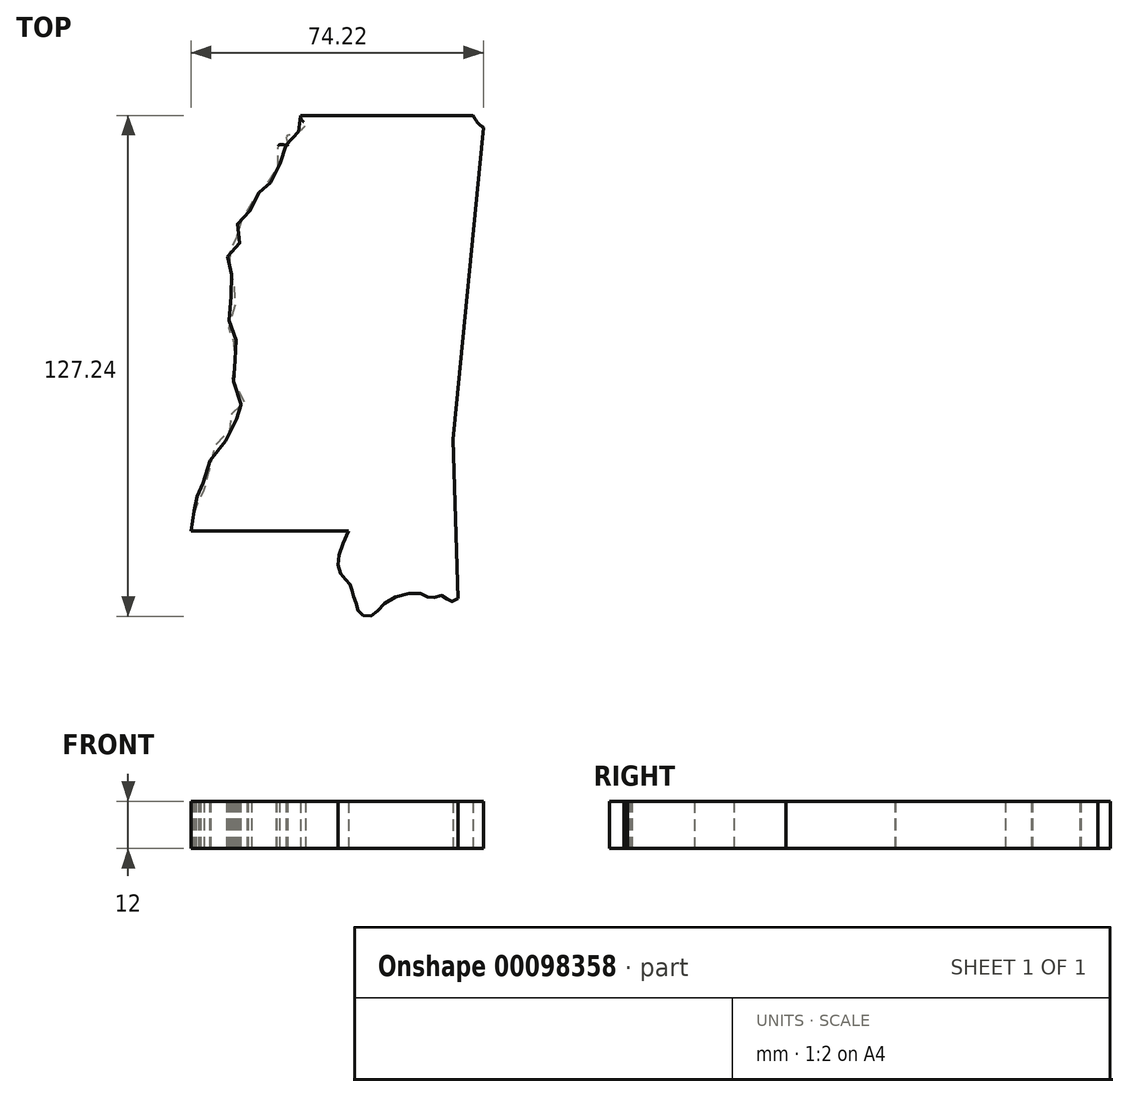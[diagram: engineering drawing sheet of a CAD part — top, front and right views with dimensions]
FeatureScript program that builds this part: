
annotation { "Feature Type Name" : "Feature", "Feature Type Description" : "" }
export const myFeature = defineFeature(function(context is Context, id is Id, definition is map)
    precondition{}
    {
        {
            var Q0;
            Q0=qCreatedBy(makeId("Top.planeOp"),FACE);
            var sketch = newSketch(context, id + "F0", { "sketchPlane" : qUnion([Q0])});
            skLineSegment(sketch, "E0", {"start": v(-12.7, 63.77) * mm, "end": v(31.18, 63.77) * mm});
            skFitSpline(sketch, "E1", {"points": [v(31.18, 63.77) * mm, v(32.21, 62.04) * mm, v(33.76, 60.7) * mm], "startDerivative": vector(1.8, -3.72) * mm, "endDerivative": vector(3.34, -2.47) * mm});
            skLineSegment(sketch, "E2", {"start": v(33.76, 60.7) * mm, "end": v(26.03, -18.61) * mm});
            skLineSegment(sketch, "E3", {"start": v(26.03, -18.61) * mm, "end": v(27.37, -58.89) * mm});
            skFitSpline(sketch, "E4", {"points": [v(27.37, -58.89) * mm, v(25.31, -59.72) * mm, v(23.35, -58.18) * mm, v(20.47, -58.89) * mm, v(17.78, -57.7) * mm, v(9.08, -59.84) * mm, v(5.6, -63.23) * mm, v(2.34, -62.72) * mm, v(1.36, -59.9) * mm, v(0.5, -57.7) * mm, v(0, -55.49) * mm, v(-2, -53.47) * mm, v(-3.17, -49.61) * mm, v(-0.53, -41.87) * mm], "startDerivative": vector(-36.12, -26.53) * mm, "endDerivative": vector(32.5, 71.75) * mm});
            skLineSegment(sketch, "E5", {"start": v(-0.53, -41.87) * mm, "end": v(-40.44, -41.87) * mm});
            skFitSpline(sketch, "E6", {"points": [v(-40.44, -41.87) * mm, v(-39.67, -39.77) * mm, v(-40.44, -38.7) * mm, v(-39.72, -37.05) * mm, v(-40.44, -35.23) * mm, v(-38.85, -34.85) * mm, v(-38.5, -34.05) * mm, v(-39.15, -32.33) * mm, v(-38.56, -31.67) * mm, v(-37.43, -31.59) * mm, v(-37.05, -30.55) * mm, v(-37.96, -28.15) * mm, v(-35.72, -26.44) * mm, v(-35.7, -23.45) * mm, v(-34.25, -20) * mm, v(-32.37, -19.7) * mm, v(-31.16, -17.3) * mm, v(-29.66, -15.02) * mm, v(-28.85, -13.64) * mm, v(-29.89, -12.26) * mm, v(-30.28, -10.96) * mm, v(-28.67, -9.86) * mm, v(-27.02, -9.23) * mm, v(-26.3, -7.13) * mm, v(-29.83, -3.53) * mm, v(-28.89, -0.89) * mm, v(-28.47, 0.56) * mm, v(-29.33, 1.72) * mm, v(-28.65, 2.87) * mm, v(-30.22, 4.64) * mm, v(-28.72, 7.26) * mm, v(-29.38, 9.32) * mm, v(-30.64, 9.26) * mm, v(-30.26, 13.36) * mm, v(-28.94, 14.62) * mm, v(-30.1, 17.48) * mm, v(-30.69, 18.55) * mm, v(-29.71, 20.5) * mm, v(-29.76, 22.92) * mm, v(-31.3, 24.16) * mm, v(-30.59, 25.58) * mm, v(-30.63, 27.17) * mm, v(-31.39, 28.43) * mm, v(-30.38, 29.35) * mm, v(-29.75, 30.33) * mm, v(-28.17, 31.25) * mm, v(-28.83, 33.24) * mm, v(-27.87, 34.55) * mm, v(-28.79, 35.9) * mm, v(-26.78, 37.23) * mm, v(-25.14, 37.45) * mm, v(-25.35, 38.95) * mm, v(-25.9, 40.42) * mm, v(-24.3, 42) * mm, v(-23.54, 44.18) * mm, v(-22.36, 43.96) * mm, v(-22.1, 45.63) * mm, v(-21.62, 46.62) * mm, v(-20.25, 46.74) * mm, v(-18.65, 47.92) * mm, v(-18.74, 49.65) * mm, v(-17.9, 51.6) * mm, v(-18.66, 53.8) * mm, v(-17.96, 56.35) * mm, v(-15.95, 56.25) * mm, v(-16.18, 58.35) * mm, v(-14.42, 59.18) * mm, v(-12.65, 60.1) * mm, v(-11.33, 61.65) * mm, v(-12.29, 62.48) * mm, v(-12.7, 63.77) * mm], "startDerivative": vector(163.3, 88.27) * mm, "endDerivative": vector(-8.55, 126.33) * mm});
            skLineSegment(sketch, "E7", {"start": v(17.74, 63.77) * mm, "end": v(17.04, -63.23) * mm, "construction": true});
            skSolve(sketch);
        }
        {
            var Q0;
            Q0 = qSketchRegion(id + "F0", true);
            extrude(context, id + "F1", {"entities" : qUnion([Q0]), "depth" : 2 * mm, "offsetDistance" : 25 * mm});
        }
        {
            var Q0;
            Q0=makeQuery(id+"F1.opExtrude","SWEPT_BODY",BODY,{"disambiguationData":[OSD([sQuery(id+"F0.wireOp",EDGE,"E0"),sQuery(id+"F0.wireOp",EDGE,"E1"),sQuery(id+"F0.wireOp",EDGE,"E2"),sQuery(id+"F0.wireOp",EDGE,"E3"),sQuery(id+"F0.wireOp",EDGE,"E4"),sQuery(id+"F0.wireOp",EDGE,"E5"),sQuery(id+"F0.wireOp",EDGE,"E6")])]});
            transform(context, id + "F2", {"entities" : qUnion([Q0]), "transformType" : TransformType.TRANSLATION_3D, "dx" : 0 * mm, "dy" : 0 * mm, "dz" : 0 * mm, "makeCopy" : true});
        }
        {
            var Q0;
            Q0=makeQuery(id+"F1.opExtrude","CAP_FACE",FACE,{"disambiguationData":[OSD([sQuery(id+"F0.wireOp",EDGE,"E0"),sQuery(id+"F0.wireOp",EDGE,"E1"),sQuery(id+"F0.wireOp",EDGE,"E2"),sQuery(id+"F0.wireOp",EDGE,"E3"),sQuery(id+"F0.wireOp",EDGE,"E4"),sQuery(id+"F0.wireOp",EDGE,"E5"),sQuery(id+"F0.wireOp",EDGE,"E6")])],"isStart":false});
            extrude(context, id + "F3", {"entities" : qUnion([Q0]), "operationType" : NewBodyOperationType.ADD, "depth" : 10 * mm, "offsetDistance" : 25 * mm});
        }
    });
